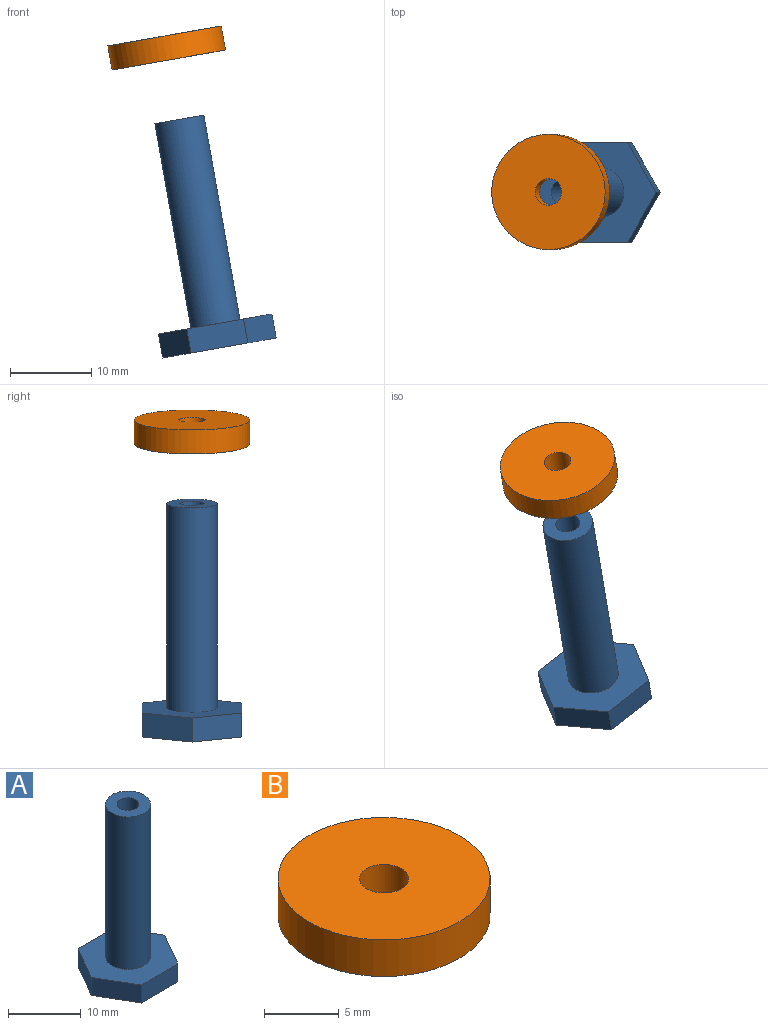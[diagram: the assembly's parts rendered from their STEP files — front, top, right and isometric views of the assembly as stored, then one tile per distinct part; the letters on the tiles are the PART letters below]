
ASSEMBLY  parts=2 mates=1
PART A: 12 faces, bbox 14.2x12.3x28.6 mm
  f0: cylinder r=3.1mm len=25.6mm, axis (0,0,-1), area 498.6mm2, adj f1,f9
  f1: plane 6.2x6.2mm, normal (0,0,1), area 23.1mm2, adj f0,f10
  f2: plane 6.15x3.55mm, normal (0.87,0.5,0), area 21.3mm2, adj f3,f7,f8,f9
  f3: plane 6.15x3.55mm, normal (0.87,-0.5,0), area 21.3mm2, adj f2,f4,f8,f9
  f4: plane 7.1x3mm, normal (0,-1,0), area 21.3mm2, adj f3,f5,f8,f9
  f5: plane 6.15x3.55mm, normal (-0.87,-0.5,0), area 21.3mm2, adj f4,f6,f8,f9
  f6: plane 6.15x3.55mm, normal (-0.87,0.5,0), area 21.3mm2, adj f5,f7,f8,f9
  f7: plane 7.1x3mm, normal (0,1,0), area 21.3mm2, adj f2,f6,f8,f9
  f8: plane 14.2x12.3mm, normal (0,0,-1), area 131mm2, adj f2,f3,f4,f5,f6,f7
  f9: plane 14.2x12.3mm, normal (0,0,1), area 100.8mm2, adj f0,f2,f3,f4,f5,f6,f7
  f10: cylinder r=1.5mm len=10mm, axis (0,0,1), area 94.2mm2, adj f1,f11
  f11: plane 3x3mm, normal (0,0,1), area 7.1mm2, adj f10
PART B: 4 faces, bbox 14.2x14.2x3 mm
  f0: cylinder r=7.1mm len=14.2mm, axis (0,0,-1), area 133.8mm2, adj f1,f2
  f1: plane 14.2x14.2mm, normal (0,0,1), area 149.8mm2, adj f0,f3
  f2: plane 14.2x14.2mm, normal (0,0,-1), area 149.8mm2, adj f0,f3
  f3: cylinder r=1.65mm len=3.3mm, axis (0,0,1), area 31.1mm2, adj f1,f2
PLACE A rot(axis=(0,-1,0),10deg) t=(-8.11,-1.9,-3.25)mm
PLACE B rot(axis=(0,-1,0),10deg) t=(-13.85,-1.9,29.3)mm
MATE slider B.f3 <-> A.f0  axis (-0.17,0,0.98) through (-13.85,-1.9,29.3)mm
